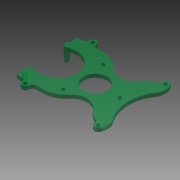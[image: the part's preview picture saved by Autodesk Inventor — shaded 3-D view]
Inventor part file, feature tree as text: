
AUTODESK INVENTOR PART (.ipt)
format: ipt  version: 2014 (Build 180170000, 170)  size: 279,552 bytes
history: native  units: in
note: dims shown in document units (in); Inventor stores cm internally (conversion verified against a paired STEP export)
features: extrude x7, fillet x7, sketch x7, pattern_circular x1
ambient origin geometry x8: Origin, YZ Plane, XZ Plane, XY Plane, X Axis, Y Axis, Z Axis, Center Point
bodies: Solid1 (feature_tree)
feature tree (22):
  extrude  "Extrusion1"  Depth=3.7in
  extrude  "Extrusion2"  Depth=1.0in
  extrude  "Extrusion3"  Depth=0.2in TaperAngle=0.0deg
  pattern_circular  "Circular Pattern1"  Count=3 Angle=360.0deg
  extrude  "Extrusion4"  Depth=0.3in
  extrude  "Extrusion5"  Depth=1.0in
  fillet  "Fillet1"  Radius=0.135in
  fillet  "Fillet2"  Radius=0.15in
  fillet  "Fillet3"  Radius=0.15in
  extrude  "Extrusion6"  Depth=0.15in
  fillet  "Fillet4"  Radius=0.15in
  fillet  "Fillet5"  Radius=0.15in
  extrude  "Extrusion7"  Depth=0.2in
  fillet  "Fillet6"  Radius=0.3in
  fillet  "Fillet7"  Radius=0.3in
  sketch  "Sketch1"  dims[d0=2.6in d1=3.7in]
  sketch  "Sketch2"  dims[d2=0.15in d3=0.0in d4=1.0in]
  sketch  "Sketch3"  dims[d5=2.0in d6=0.2in d7=0.0in]
  sketch  "Sketch4"  dims[d8=0.135in]
  sketch  "Sketch5"  dims[d10=0.2in d11=0.0in d12=1.1811in d13=360.0deg]
  sketch  "Sketch6"  dims[d15=1.0in d16=0.3in]
  sketch  "Sketch7"  dims[d18=2.9in d20=3.0in d21=0.135in d22=0.15in d23=0.15in d24=0.15in d25=0.15in d26=0.0in d27=0.15in d28=0.2in d29=0.3in d30=0.3in d31=0.7in d32=0.0in d33=0.125in d34=0.125in d35=0.05in d36=0.15in d37=0.15in d38=0.25in d39=0.25in d40=0.25in d41=0.25in d42=0.7in d43=0.0in d44=0.5in d45=0.05in d46=0.25in d47=0.25in d48=0.25in d49=0.25in d50=0.25in d51=0.25in d52=0.7in d53=0.0in d54=1.0in d55=1.0in]
